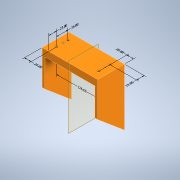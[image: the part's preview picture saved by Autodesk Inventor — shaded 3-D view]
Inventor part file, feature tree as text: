
AUTODESK INVENTOR PART (.ipt)
format: ipt  version: 2022.2 (Build 262287000, 287)  size: 408,064 bytes
history: native  units: mm
features: sketch x24, extrude x10, other x7, hole x6, loft x4, split x1, projected_geometry x1
ambient origin geometry x8: Origin, YZ Plane, XZ Plane, XY Plane, X Axis, Y Axis, Z Axis, Center Point
bodies: Body1 (feature_tree)
feature tree (53):
  other  "Annotations"
  extrude  "Extrusion8"  Depth=166.0mm
  extrude  "armsForCameraCase"  TaperAngle=0.0deg  [1 undecoded]
  extrude  "Extrusion10"  Depth=8.0mm
  extrude  "Extrusion11"  Depth=150.0mm TaperAngle=0.0deg
  extrude  "Extrusion12"  Depth=8.0mm
  hole  "HolesForAttchingToLowerCase"  [1 undecoded]
  extrude  "Extrusion13"  Depth=104.1375mm
  hole  "HoleForLeftSideOf2x4"  [1 undecoded]
  hole  "HolesForRightSideOf2x4"  [1 undecoded]
  extrude  "Extrusion14"  TaperAngle=0.0deg  [1 undecoded]
  extrude  "Extrusion15"  Depth=26.108146mm
  extrude  "Extrusion16"  Depth=8.0mm
  loft  "Loft5"
  loft  "Loft6"
  loft  "Loft7"
  loft  "Loft8"
  split  "Split3"
  extrude  "ExtrusionForMatingUpperHalf"  TaperAngle=0.0deg  [1 undecoded]
  hole  "HoleForNumber10Screws"  [1 undecoded]
  hole  "HoleForInserts"  [1 undecoded]
  hole  "Hole8"  [1 undecoded]
  sketch  "Sketch8"  dims[d28=80.0mm d29=166.0mm]
  sketch  "Sketch9"  dims[d30=8.0mm d31=0.0mm]
  sketch  "Sketch10"  dims[d32=8.0mm d33=8.0mm]
  sketch  "Sketch11"  dims[d34=150.0mm d35=0.0mm d37=125.0mm d38=0.0mm]
  sketch  "Sketch12"  dims[d39=-2.617994mm d40=8.0mm]
  sketch  "Sketch13"  dims[d42=8.0mm d44=20.32mm]
  sketch  "Sketch14"  dims[d45=20.32mm d46=104.1375mm]
  sketch  "Sketch15"  dims[d47=0.0mm d48=6.981317mm]
  sketch  "Sketch16"  dims[d49=20.0mm d50=0.0mm d51=100.0mm]
  sketch  "Sketch17"  dims[d52=6.7564mm d53=6.0mm d54=15.875mm d55=4.826mm d56=14.3117mm d57=8.0mm d58=20.594885mm d59=0.0mm d60=0.0mm]
  sketch  "Sketch18"  dims[d62=26.108146mm d63=26.108146mm]
  projected_geometry  "Projected Loop3"
  sketch  "Sketch19"  dims[d64=25.0mm]
  sketch  "Sketch27"  dims[d65=4.496mm d66=6.0mm d67=8.433mm d68=2.794mm d69=14.3117mm d70=8.0mm d71=0.0mm d72=30.0mm d74=20.0mm d75=30.0mm d77=20.0mm]
  sketch  "Sketch28"  dims[d80=20.0mm d81=15.0mm]
  sketch  "Sketch29"  dims[d82=30.0mm d84=20.0mm d85=30.0mm d87=20.0mm d90=20.0mm]
  sketch  "Sketch30"  dims[d91=4.496mm d92=6.0mm d93=8.433mm d94=2.0mm d95=14.3117mm d96=8.0mm d97=0.0mm d98=8.0mm]
  sketch  "Sketch31"  dims[d99=8.0mm d101=8.0mm]
  sketch  "Sketch32"  dims[d102=8.0mm d103=0.0mm d104=0.0mm]
  sketch  "Sketch33"  dims[d105=8.0mm d107=8.0mm]
  sketch  "Sketch34"  dims[d108=16.0mm d109=8.0mm]
  sketch  "Sketch37"  dims[d110=0.0mm d111=0.0mm d112=8.0mm]
  sketch  "Sketch38"  dims[d113=16.0mm]
  sketch  "SketchForHeatSetInserts"  dims[d115=8.0mm d116=0.0mm d117=0.0mm d152=30.0mm d153=30.0mm d154=0.0mm d155=90.0deg d156=0.0mm d157=90.0deg d158=30.0mm d159=30.0mm d160=0.0mm d161=90.0deg d162=0.0mm d163=90.0deg d164=39.0mm d165=30.0mm d166=0.0mm d167=90.0deg d168=0.0mm d169=90.0deg d170=30.0mm d171=30.0mm d172=0.0mm d173=90.0deg d174=0.0mm d175=90.0deg d185=12.5mm d186=0.0mm d187=5.1054mm d188=6.0mm d189=4.0mm d190=2.0mm d191=90.0deg d192=8.0mm d193=0.0mm d194=6.32mm d195=6.0mm d196=6.5278mm d197=7.41mm d198=14.3117mm d199=9.525mm d200=0.0mm d210=33.242mm d211=33.242mm d212=5.1054mm d213=6.0mm d214=4.0mm d215=2.0mm d216=90.0deg d217=50.0mm d218=0.0mm d219=34.0mm d220=126.0mm d221=23.0mm d222=0.940495mm d223=23.0mm d224=4.5884mm d225=20.0mm d226=6.283396mm d227=20.0mm d73=0.0625mm]
  sketch  "Sketch42"  dims[d114=8.0mm]
  other  "Linear Dimension 1"
  other  "Linear Dimension 2"
  other  "Linear Dimension 3"
  other  "Linear Dimension 4"
  other  "Linear Dimension 5"
  other  "Linear Dimension 6"
note: 9 required parameter values undecoded (feature->parameter linkage not recoverable at this tier; creation-order binding heuristic only, values carry confidence <= 0.55)
